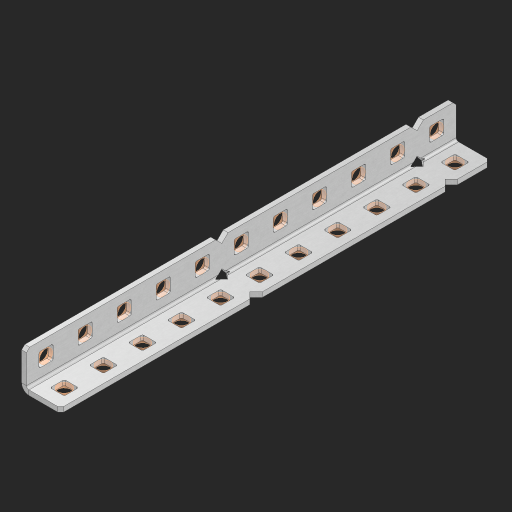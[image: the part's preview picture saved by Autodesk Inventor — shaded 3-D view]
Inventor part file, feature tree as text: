
AUTODESK INVENTOR PART (.ipt)
format: ipt  version: 2023 (Build 270158000, 158)  size: 637,952 bytes
history: native  units: in
note: dims shown in document units (in); Inventor stores cm internally (conversion verified against a paired STEP export)
features: other x28, extrude x23, sheet_metal_op x8, sketch x5, pattern_linear x1, mirror x1, chamfer x1
ambient origin geometry x8: Origin, YZ Plane, XZ Plane, XY Plane, X Axis, Y Axis, Z Axis, Center Point
bodies: Solid1 (feature_tree), Body (feature_tree)
feature tree (67):
  sheet_metal_op  "Flanges"
  sheet_metal_op  "Body Pattern"
  other  "Arc Length"
  pattern_linear  "Notch Pattern"  Spacing1=0.125in  [1 undecoded]
  other  "Diagonal Plane"
  mirror  "Everything Mirrored"
  chamfer  "End Chamfer"
  sketch  "Sketch1"  dims[d0=0.5in]
  other  "Plate1"
  sketch  "Sketch2"  dims[d1=5.5in]
  other  "Plate2"
  sheet_metal_op  "Bend1"
  sheet_metal_op  "Corner1"
  sketch  "Sketch8"  dims[d2=0.0625in]
  sketch  "Sketch9"  dims[d3=0.0625in]
  other  "Srf91"
  sheet_metal_op  "Body Pattern Sketch"
  other  "Srf92"
  sketch  "Sketch13"  dims[d4=0.0312in d5=0.125in d6=0.0625in d7=0.5in d8=90.0deg d9=0.0312in d10=0.25in d11=0.0625in d12=0.0625in d49=0.182in d50=0.02in d52=0.25in d53=0.0625in d54=0.0in d55=0.172in d56=1.0in d57=0.0in d85=0.1473in d86=0.1782in d89=0.0625in d90=0.0in d91=0.04in d92=0.0491in d95=2.5in d96=0.04in d97=0.25in d98=45.0deg d123=0.204in d126=0.0491in d127=0.1473in d128=0.08in d129=0.04in d130=2.5in d131=4.3307in d133=0.5in d134=0.3937in d136=1.0in]
  other  "Srf856"
  other  "Srf857"
  other  "Srf858"
  other  "Srf859"
  other  "Srf860"
  other  "Srf861"
  other  "Srf1275"
  other  "Srf1276"
  other  "Srf1278"
  other  "Srf1279"
  other  "Srf1280"
  other  "Srf1281"
  other  "Srf1282"
  other  "Srf1283"
  other  "Srf1383"
  other  "Srf1384"
  other  "Srf1385"
  other  "Srf1386"
  other  "Srf1475"
  other  "Srf1476"
  other  "Srf1477"
  other  "Srf1478"
  sheet_metal_op  "Body Stamp"
  sheet_metal_op  "Body Circle"
  sheet_metal_op  "Notch"
  extrude  "ExtrusionSrf92"  Depth=0.0625in
  extrude  "ExtrusionSrf856"  Depth=0.5in TaperAngle=90.0deg
  extrude  "ExtrusionSrf857"  Depth=0.25in
  extrude  "ExtrusionSrf858"  Depth=0.0625in
  extrude  "ExtrusionSrf859"  Depth=0.0625in
  extrude  "ExtrusionSrf860"  Depth=0.3937in
  extrude  "ExtrusionSrf861"  Depth=0.02in
  extrude  "ExtrusionSrf1275"  Depth=0.25in
  extrude  "ExtrusionSrf1276"  Depth=0.0625in
  extrude  "ExtrusionSrf1277"  TaperAngle=0.0deg  [1 undecoded]
  extrude  "ExtrusionSrf1278"  Depth=0.3937in
  extrude  "ExtrusionSrf1279"  Depth=0.3937in TaperAngle=0.0deg
  extrude  "ExtrusionSrf1280"  Depth=0.3937in
  extrude  "ExtrusionSrf1281"  Depth=0.3937in
  extrude  "ExtrusionSrf1282"  Depth=0.0625in
  extrude  "ExtrusionSrf1383"  Depth=0.3937in TaperAngle=0.0deg
  extrude  "ExtrusionSrf1384"  Depth=0.3937in
  extrude  "ExtrusionSrf1385"  Depth=0.25in TaperAngle=45.0deg
  extrude  "ExtrusionSrf1386"  Depth=0.3937in
  extrude  "ExtrusionSrf1475"  Depth=0.3937in
  extrude  "ExtrusionSrf1476"  Depth=0.3937in
  extrude  "ExtrusionSrf1477"  Depth=0.3937in
  extrude  "ExtrusionSrf1478"  Depth=0.3937in
note: 2 required parameter values undecoded (feature->parameter linkage not recoverable at this tier; creation-order binding heuristic only, values carry confidence <= 0.55)
